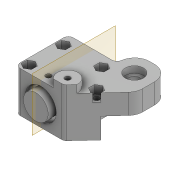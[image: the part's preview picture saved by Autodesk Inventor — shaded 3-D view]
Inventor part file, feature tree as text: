
AUTODESK INVENTOR PART (.ipt)
format: ipt  version: 2022 (Build 260153000, 153)  size: 356,864 bytes
history: native  units: mm
features: extrude x11, sketch x10, projected_geometry x8, fillet x3, plane x1
ambient origin geometry x8: Origin, YZ Plane, XZ Plane, XY Plane, X Axis, Y Axis, Z Axis, Center Point
bodies: Solid1 (feature_tree)
feature tree (33):
  extrude  "Extrusion1"  Depth=12.2mm
  extrude  "Extrusion2"  Depth=2.0mm
  extrude  "Extrusion3"  Depth=2.0mm TaperAngle=0.0deg
  plane  "Work Plane1"
  extrude  "Extrusion4"  Depth=3.0mm
  extrude  "Extrusion6"  Depth=7.0mm
  sketch  "Sketch6"  dims[d12=16.0mm d14=7.0mm]
  extrude  "Extrusion7"  Depth=6.0mm
  extrude  "Extrusion8"  Depth=4.1mm
  fillet  "Fillet1"  Radius=3.0mm
  fillet  "Fillet3"  Radius=4.1mm
  fillet  "Fillet4"  Radius=1.5mm
  extrude  "Extrusion9"  Depth=4.1mm
  extrude  "Extrusion10"  Depth=4.1mm
  extrude  "Extrusion11"  Depth=3.2mm TaperAngle=0.0deg
  extrude  "Extrusion12"  Depth=2.1mm
  sketch  "Sketch1"  dims[d0=9.8mm d1=12.2mm]
  sketch  "Sketch2"  dims[d3=3.0mm d4=2.0mm]
  projected_geometry  "Projected Loop1"
  sketch  "Sketch3"  dims[d5=18.0mm d6=0.0mm d7=2.0mm d8=0.0mm]
  projected_geometry  "Projected Loop2"
  sketch  "Sketch5"  dims[d9=3.0mm d10=0.0mm d11=4.2mm]
  projected_geometry  "Projected Loop3"
  projected_geometry  "Projected Loop4"
  sketch  "Sketch8"  dims[d15=7.0mm d16=6.0mm]
  projected_geometry  "Projected Loop6"
  sketch  "Sketch9"  dims[d17=8.0mm d18=0.0mm d19=4.1mm d21=3.0mm d22=4.1mm d23=1.5mm]
  projected_geometry  "Projected Loop7"
  sketch  "Sketch10"  dims[d26=1.0mm d27=0.0mm d28=4.1mm]
  sketch  "Sketch11"  dims[d29=4.1mm d30=1.5mm]
  projected_geometry  "Projected Loop8"
  sketch  "Sketch12"  dims[d31=1.5mm d32=3.2mm d33=0.0mm d34=2.1mm d35=2.1mm d36=2.1mm d37=2.1mm d38=100.0mm d39=0.0mm d40=6.0mm d42=2.0mm d43=4.0mm d44=1.5mm d45=4.1mm d46=2.1mm d47=8.0mm d48=8.0mm d49=2.1mm d50=3.0mm d51=4.1mm d52=7.1mm d53=2.6mm d54=0.0mm d55=7.1mm d56=2.6mm d57=0.0mm d59=8.2mm d60=0.0mm d62=3.0mm d63=0.0mm d64=3.0mm d65=0.0mm d67=8.0mm]
  projected_geometry  "Projected Loop9"
